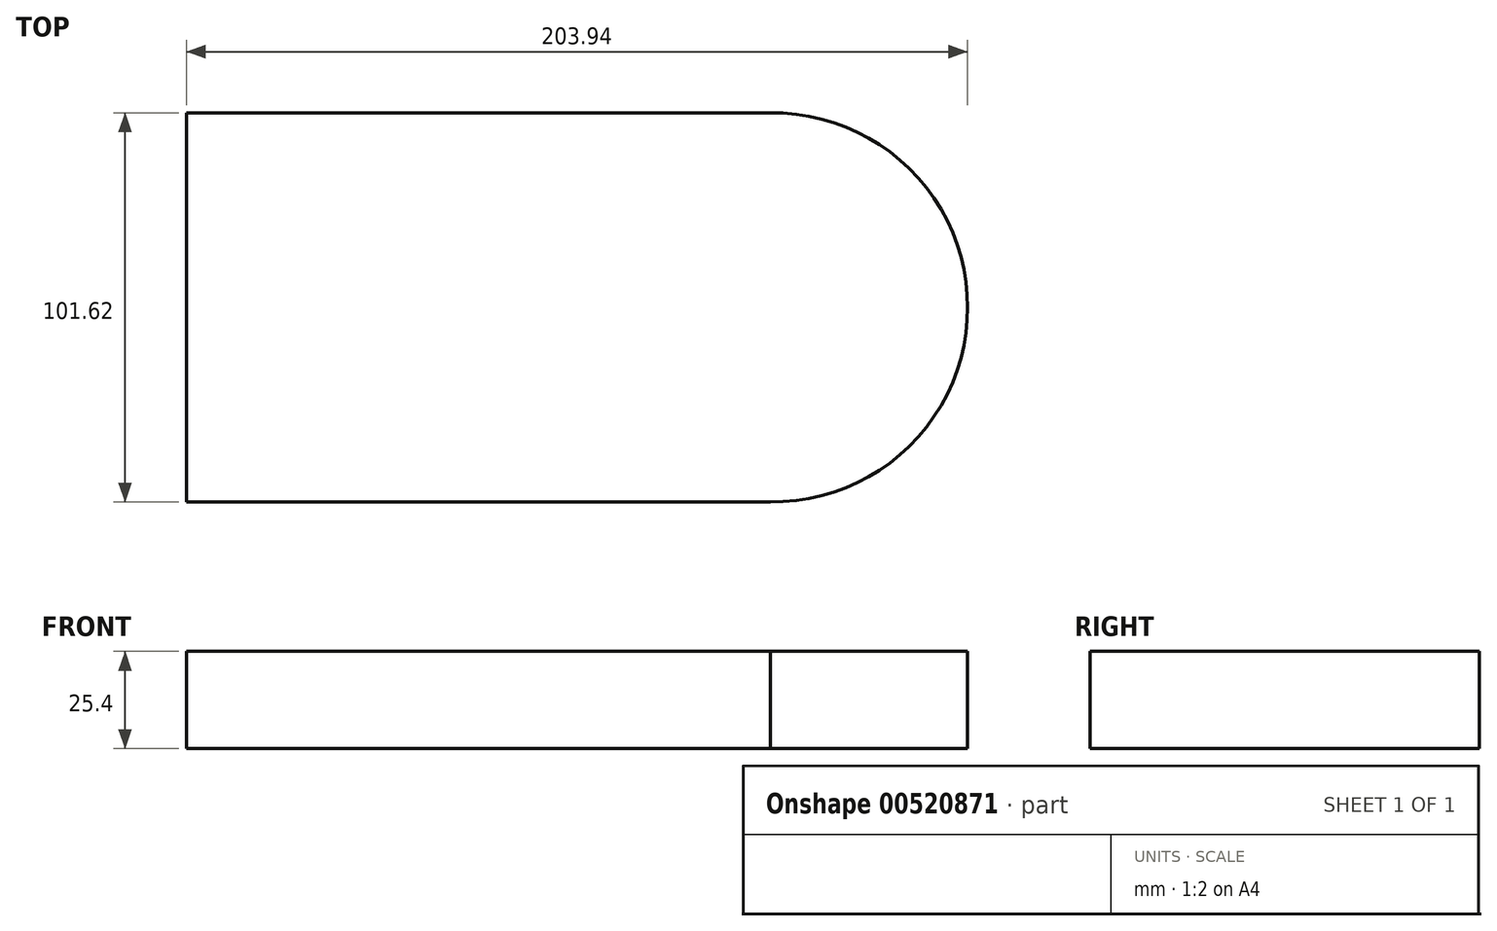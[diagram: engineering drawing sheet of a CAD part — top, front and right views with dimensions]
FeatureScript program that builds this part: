
annotation { "Feature Type Name" : "Feature", "Feature Type Description" : "" }
export const myFeature = defineFeature(function(context is Context, id is Id, definition is map)
    precondition{}
    {
        {
            var Q0;
            Q0=qCreatedBy(makeId("Top.planeOp"),FACE);
            var sketch = newSketch(context, id + "F0", { "sketchPlane" : qUnion([Q0])});
            skLineSegment(sketch, "E0.bottom", {"start": v(-76.2, 50.8) * mm, "end": v(76.2, 50.8) * mm});
            skLineSegment(sketch, "E0.top", {"start": v(-76.2, -50.8) * mm, "end": v(76.2, -50.8) * mm});
            skLineSegment(sketch, "E0.left", {"start": v(-76.2, 50.8) * mm, "end": v(-76.2, -50.8) * mm});
            skLineSegment(sketch, "E0.right", {"start": v(76.2, 50.8) * mm, "end": v(76.2, -50.8) * mm});
            skPoint(sketch, "E0.middle", {"position": v(0, 0) * mm});
            skSolve(sketch);
        }
        {
            var Q0;
            Q0 = qSketchRegion(id + "F0", true);
            extrude(context, id + "F1", {"entities" : qUnion([Q0]), "depth" : 25.4 * mm, "offsetDistance" : 25.4 * mm});
        }
        {
            var Q0;
            Q0=makeQuery(id+"F1.opExtrude","CAP_FACE",FACE,{"disambiguationData":[OSD([sQuery(id+"F0.wireOp",EDGE,"E0.bottom"),sQuery(id+"F0.wireOp",EDGE,"E0.top"),sQuery(id+"F0.wireOp",EDGE,"E0.left"),sQuery(id+"F0.wireOp",EDGE,"E0.right")])],"isStart":false});
            var sketch = newSketch(context, id + "F2", { "sketchPlane" : qUnion([Q0])});
            skArc(sketch, "E1", {"start": v(76.2, -50.8) * mm, "mid": v(127.74, 0) * mm, "end": v(76.2, 50.8) * mm});
            skSolve(sketch);
        }
        {
            var Q0;
            Q0=makeQuery(id+"F2.imprint","IMPRINT",FACE,{"disambiguationData":[TD([[makeQuery(id+"F2.imprint","IMPRINT",EDGE,{"derivedFrom":sQuery(id+"F2.wireOp",EDGE,"E1")}),1.0]])]});
            extrude(context, id + "F3", {"entities" : qUnion([Q0]), "operationType" : NewBodyOperationType.ADD, "oppositeDirection" : true, "depth" : 25.4 * mm, "offsetDistance" : 25.4 * mm});
        }
    });
